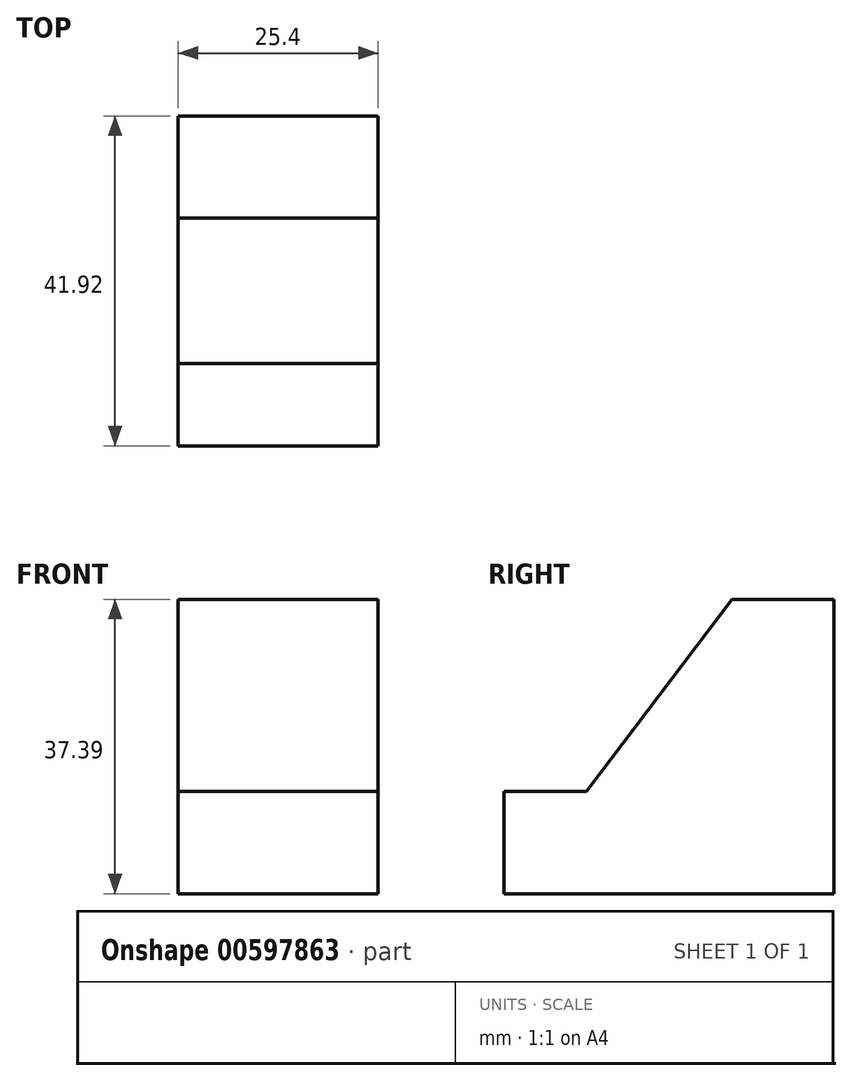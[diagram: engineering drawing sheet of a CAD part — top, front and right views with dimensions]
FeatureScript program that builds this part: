
annotation { "Feature Type Name" : "Feature", "Feature Type Description" : "" }
export const myFeature = defineFeature(function(context is Context, id is Id, definition is map)
    precondition{}
    {
        {
            var Q0;
            Q0=qCreatedBy(makeId("Right.planeOp"),FACE);
            var sketch = newSketch(context, id + "F0", { "sketchPlane" : qUnion([Q0])});
            skLineSegment(sketch, "E0", {"start": v(0, 0) * mm, "end": v(0, 37.4) * mm});
            skLineSegment(sketch, "E1", {"start": v(0, 37.4) * mm, "end": v(-12.99, 37.4) * mm});
            skLineSegment(sketch, "E2", {"start": v(0, 0) * mm, "end": v(-41.92, 0) * mm});
            skLineSegment(sketch, "E3", {"start": v(-41.92, 0) * mm, "end": v(-41.92, 12.99) * mm});
            skLineSegment(sketch, "E4", {"start": v(-41.92, 12.99) * mm, "end": v(-31.46, 12.99) * mm});
            skLineSegment(sketch, "E5", {"start": v(-31.46, 12.99) * mm, "end": v(-12.99, 37.4) * mm});
            skSolve(sketch);
        }
        {
            var Q0;
            Q0=makeQuery(id+"F0.imprint","IMPRINT",FACE,{"disambiguationData":[TD([[makeQuery(id+"F0.imprint","IMPRINT",EDGE,{"derivedFrom":sQuery(id+"F0.wireOp",EDGE,"E0")}),1.0]])]});
            extrude(context, id + "F1", {"entities" : qUnion([Q0]), "depth" : 25.4 * mm, "offsetDistance" : 25.4 * mm});
        }
    });
